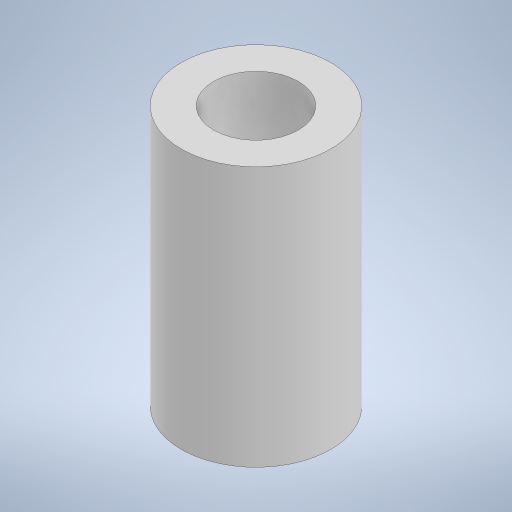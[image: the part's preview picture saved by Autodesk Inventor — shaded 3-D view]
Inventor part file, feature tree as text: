
AUTODESK INVENTOR PART (.ipt)
format: ipt  version: 2024.2 (Build 282272000, 272)  size: 510,976 bytes
history: native  units: in
note: dims shown in document units (in); Inventor stores cm internally (conversion verified against a paired STEP export)
features: extrude x1, sketch x1
ambient origin geometry x8: Origin, YZ Plane, XZ Plane, XY Plane, X Axis, Y Axis, Z Axis, Center Point
bodies: Solid1 (feature_tree)
feature tree (2):
  extrude  "Extrusion1"  Depth=1.0in
  sketch  "Sketch1"  dims[d0=0.325in d2=0.125in d3=1.0in d4=0.0in]
